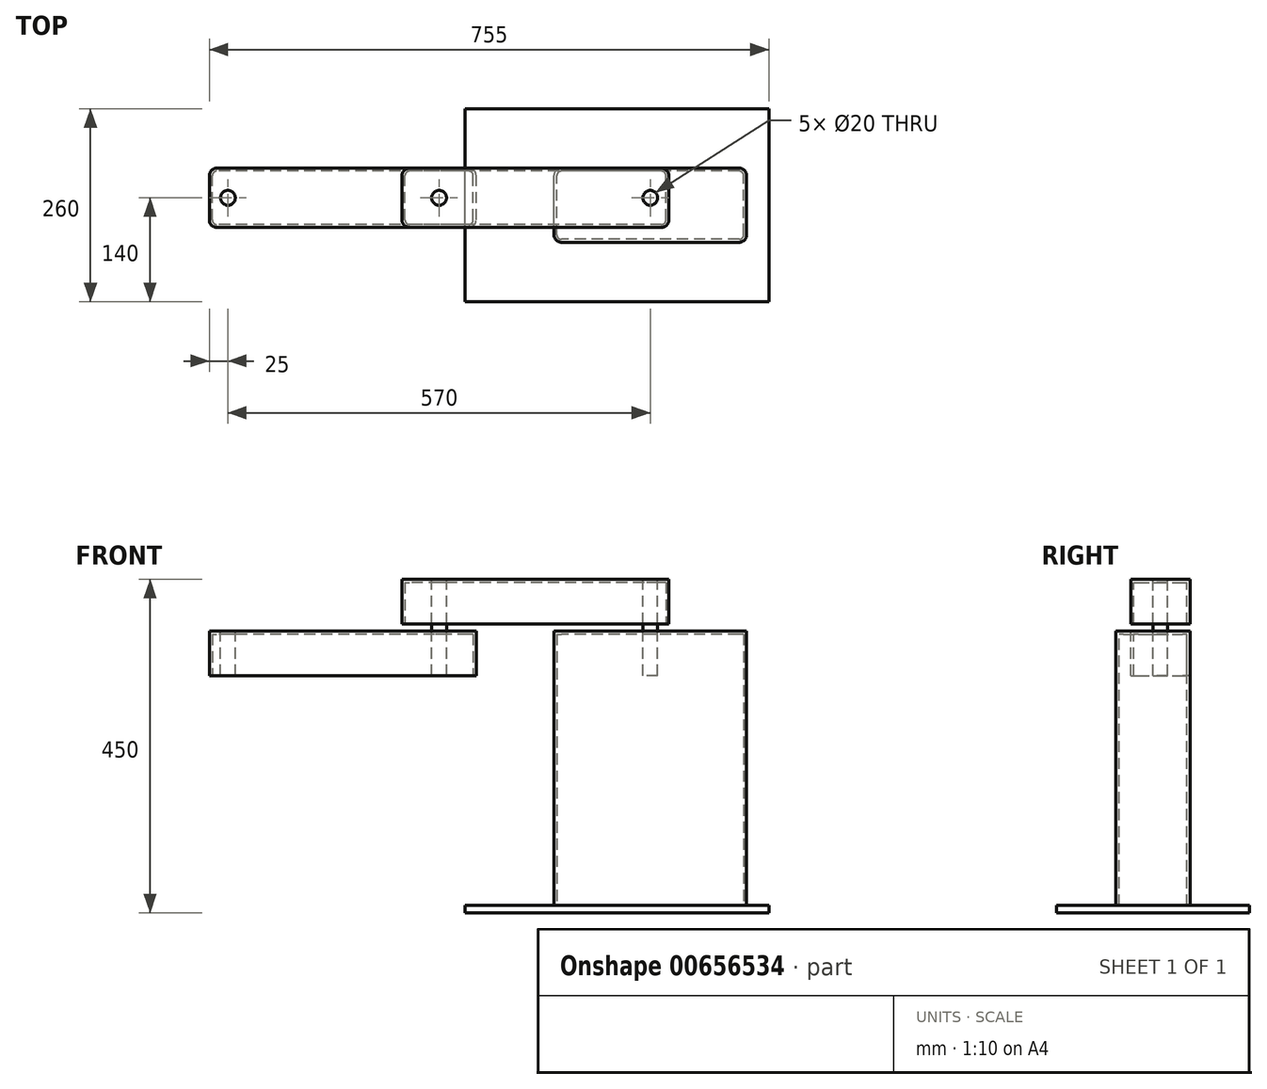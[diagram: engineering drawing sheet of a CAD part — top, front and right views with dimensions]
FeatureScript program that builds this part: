
annotation { "Feature Type Name" : "Feature", "Feature Type Description" : "" }
export const myFeature = defineFeature(function(context is Context, id is Id, definition is map)
    precondition{}
    {
        {
            var Q0;
            Q0=qCreatedBy(makeId("Top.planeOp"),FACE);
            var sketch = newSketch(context, id + "F0", { "sketchPlane" : qUnion([Q0])});
            skLineSegment(sketch, "E0.bottom", {"start": v(180, -40) * mm, "end": v(-180, -40) * mm});
            skLineSegment(sketch, "E0.top", {"start": v(180, 40) * mm, "end": v(-180, 40) * mm});
            skLineSegment(sketch, "E0.left", {"start": v(180, -40) * mm, "end": v(180, 40) * mm});
            skLineSegment(sketch, "E0.right", {"start": v(-180, -40) * mm, "end": v(-180, 40) * mm});
            skPoint(sketch, "E0.middle", {"position": v(0, 0) * mm});
            skPoint(sketch, "E1.center.orphan", {"position": v(-130, 0) * mm});
            skPoint(sketch, "E2.center.orphan", {"position": v(155, 0) * mm});
            skSolve(sketch);
        }
        {
            var Q0;
            Q0=makeQuery(id+"F0.imprint","IMPRINT",FACE,{"disambiguationData":[TD([[makeQuery(id+"F0.imprint","IMPRINT",EDGE,{"derivedFrom":sQuery(id+"F0.wireOp",EDGE,"E0.bottom")}),-1.0]])]});
            extrude(context, id + "F1", {"entities" : qUnion([Q0]), "oppositeDirection" : true, "depth" : 60 * mm, "offsetDistance" : 25 * mm});
        }
        {
            var Q0;
            Q0=makeQuery(id+"F1.opExtrude","CAP_FACE",FACE,{"disambiguationData":[OSD([sQuery(id+"F0.wireOp",EDGE,"E0.bottom"),sQuery(id+"F0.wireOp",EDGE,"E0.top"),sQuery(id+"F0.wireOp",EDGE,"E0.left"),sQuery(id+"F0.wireOp",EDGE,"E0.right"),sQuery(id+"F0.wireOp",EDGE,"E2"),sQuery(id+"F0.wireOp",EDGE,"E1")])],"isStart":true});
            cPlane(context, id + "F2", {"entities" : qUnion([Q0]), "cplaneType" : CPlaneType.OFFSET, "offset" : 70 * mm, "oppositeDirection" : true, "width" : 150 * mm, "height" : 150 * mm});
        }
        {
            var Q0;
            Q0=qCreatedBy(id+"F2.planeOp",FACE);
            var sketch = newSketch(context, id + "F3", { "sketchPlane" : qUnion([Q0])});
            skLineSegment(sketch, "E3.bottom", {"start": v(285, -60) * mm, "end": v(25, -60) * mm});
            skLineSegment(sketch, "E3.top", {"start": v(285, 40) * mm, "end": v(25, 40) * mm});
            skLineSegment(sketch, "E3.left", {"start": v(285, -60) * mm, "end": v(285, 40) * mm});
            skLineSegment(sketch, "E3.right", {"start": v(25, -60) * mm, "end": v(25, 40) * mm});
            skPoint(sketch, "E3.middle", {"position": v(155, -10) * mm});
            skLineSegment(sketch, "E4.0", {"start": v(180, -40) * mm, "end": v(180, 40) * mm, "construction": true});
            skSolve(sketch);
        }
        {
            var Q0;
            Q0=makeQuery(id+"F3.imprint","IMPRINT",FACE,{"disambiguationData":[TD([[makeQuery(id+"F3.imprint","IMPRINT",EDGE,{"derivedFrom":sQuery(id+"F3.wireOp",EDGE,"E3.bottom")}),-1.0]])]});
            extrude(context, id + "F4", {"entities" : qUnion([Q0]), "oppositeDirection" : true, "depth" : 370 * mm, "offsetDistance" : 25 * mm});
        }
        {
            var Q0;
            Q0=makeQuery(id+"F4.opExtrude","CAP_FACE",FACE,{"disambiguationData":[OSD([sQuery(id+"F3.wireOp",EDGE,"E3.bottom"),sQuery(id+"F3.wireOp",EDGE,"E3.top"),sQuery(id+"F3.wireOp",EDGE,"E3.left"),sQuery(id+"F3.wireOp",EDGE,"E3.right")])],"isStart":false});
            var sketch = newSketch(context, id + "F5", { "sketchPlane" : qUnion([Q0])});
            skLineSegment(sketch, "E5.bottom", {"start": v(315, 140) * mm, "end": v(-95, 140) * mm});
            skLineSegment(sketch, "E5.top", {"start": v(315, -120) * mm, "end": v(-95, -120) * mm});
            skLineSegment(sketch, "E5.left", {"start": v(315, 140) * mm, "end": v(315, -120) * mm});
            skLineSegment(sketch, "E5.right", {"start": v(-95, 140) * mm, "end": v(-95, -120) * mm});
            skSolve(sketch);
        }
        {
            var Q0;
            Q0=makeQuery(id+"F5.imprint","IMPRINT",FACE,{"disambiguationData":[TD([[makeQuery(id+"F5.imprint","IMPRINT",EDGE,{"derivedFrom":sQuery(id+"F5.wireOp",EDGE,"E5.bottom")}),1.0]])]});
            var Q1;
            Q1=makeQuery(id+"F5.imprint","IMPRINT",FACE,{"disambiguationData":[TD([[makeQuery(id+"F5.imprint","IMPRINT",EDGE,{"derivedFrom":makeQuery(id+"F4.opExtrude","CAP_EDGE",EDGE,{"disambiguationData":[OSD([sQuery(id+"F3.wireOp",EDGE,"E3.bottom")])],"isStart":false})}),1.0]])]});
            extrude(context, id + "F6", {"entities" : qUnion([Q0, Q1]), "depth" : 10 * mm, "offsetDistance" : 25 * mm});
        }
        {
            var Q0;
            Q0=makeQuery(id+"F4.opExtrude","CAP_FACE",FACE,{"disambiguationData":[OSD([sQuery(id+"F3.wireOp",EDGE,"E3.bottom"),sQuery(id+"F3.wireOp",EDGE,"E3.top"),sQuery(id+"F3.wireOp",EDGE,"E3.left"),sQuery(id+"F3.wireOp",EDGE,"E3.right")])],"isStart":true});
            var sketch = newSketch(context, id + "F7", { "sketchPlane" : qUnion([Q0])});
            skLineSegment(sketch, "E6.bottom", {"start": v(-80, -40) * mm, "end": v(-440, -40) * mm});
            skLineSegment(sketch, "E6.top", {"start": v(-80, 40) * mm, "end": v(-440, 40) * mm});
            skLineSegment(sketch, "E6.left", {"start": v(-80, -40) * mm, "end": v(-80, 40) * mm});
            skLineSegment(sketch, "E6.right", {"start": v(-440, -40) * mm, "end": v(-440, 40) * mm});
            skLineSegment(sketch, "E7.0", {"start": v(-180, -40) * mm, "end": v(-180, 40) * mm, "construction": true});
            skPoint(sketch, "E8.0.center.orphan", {"position": v(-130, 0) * mm});
            skSolve(sketch);
        }
        {
            var Q0;
            Q0=makeQuery(id+"F7.imprint","IMPRINT",FACE,{"disambiguationData":[TD([[makeQuery(id+"F7.imprint","IMPRINT",EDGE,{"derivedFrom":sQuery(id+"F7.wireOp",EDGE,"E6.bottom")}),-1.0]])]});
            extrude(context, id + "F8", {"entities" : qUnion([Q0]), "oppositeDirection" : true, "depth" : 60 * mm, "offsetDistance" : 25 * mm});
        }
        {
            var Q0;
            Q0=makeQuery(id+"F1.opExtrude","CAP_FACE",FACE,{"disambiguationData":[OSD([sQuery(id+"F0.wireOp",EDGE,"E0.bottom"),sQuery(id+"F0.wireOp",EDGE,"E0.top"),sQuery(id+"F0.wireOp",EDGE,"E0.left"),sQuery(id+"F0.wireOp",EDGE,"E0.right")])],"isStart":true});
            var sketch = newSketch(context, id + "F9", { "sketchPlane" : qUnion([Q0])});
            skPoint(sketch, "E9.0", {"position": v(-440, 0) * mm});
            skPoint(sketch, "E10.0", {"position": v(-180, 0) * mm});
            skPoint(sketch, "E11.0", {"position": v(180, 0) * mm});
            skLineSegment(sketch, "E12", {"start": v(-440, 0) * mm, "end": v(180, 0) * mm, "construction": true});
            skCircle(sketch, "E13", {"center": v(-415, 0) * mm, "radius": 10 * mm});
            skCircle(sketch, "E14", {"center": v(-130, 0) * mm, "radius": 10 * mm});
            skCircle(sketch, "E15", {"center": v(155, 0) * mm, "radius": 10 * mm});
            skSolve(sketch);
        }
        {
            var Q0;
            Q0=makeQuery(id+"F8.opExtrude","SWEPT_EDGE",EDGE,{"disambiguationData":[OSD([sQuery(id+"F7.wireOp",EDGE,"E6.bottom"),sQuery(id+"F7.wireOp",EDGE,"E6.right")])]});
            var Q1;
            Q1=makeQuery(id+"F8.opExtrude","SWEPT_EDGE",EDGE,{"disambiguationData":[OSD([sQuery(id+"F7.wireOp",EDGE,"E6.top"),sQuery(id+"F7.wireOp",EDGE,"E6.right")])]});
            var Q2;
            Q2=makeQuery(id+"F8.opExtrude","SWEPT_EDGE",EDGE,{"disambiguationData":[OSD([sQuery(id+"F7.wireOp",EDGE,"E6.top"),sQuery(id+"F7.wireOp",EDGE,"E6.left")])]});
            var Q3;
            Q3=makeQuery(id+"F8.opExtrude","SWEPT_EDGE",EDGE,{"disambiguationData":[OSD([sQuery(id+"F7.wireOp",EDGE,"E6.bottom"),sQuery(id+"F7.wireOp",EDGE,"E6.left")])]});
            var Q4;
            Q4=makeQuery(id+"F1.opExtrude","SWEPT_EDGE",EDGE,{"disambiguationData":[OSD([sQuery(id+"F0.wireOp",EDGE,"E0.bottom"),sQuery(id+"F0.wireOp",EDGE,"E0.right")])]});
            var Q5;
            Q5=makeQuery(id+"F1.opExtrude","SWEPT_EDGE",EDGE,{"disambiguationData":[OSD([sQuery(id+"F0.wireOp",EDGE,"E0.bottom"),sQuery(id+"F0.wireOp",EDGE,"E0.left")])]});
            var Q6;
            Q6=makeQuery(id+"F1.opExtrude","SWEPT_EDGE",EDGE,{"disambiguationData":[OSD([sQuery(id+"F0.wireOp",EDGE,"E0.top"),sQuery(id+"F0.wireOp",EDGE,"E0.left")])]});
            var Q7;
            Q7=makeQuery(id+"F1.opExtrude","SWEPT_EDGE",EDGE,{"disambiguationData":[OSD([sQuery(id+"F0.wireOp",EDGE,"E0.top"),sQuery(id+"F0.wireOp",EDGE,"E0.right")])]});
            var Q8;
            Q8=makeQuery(id+"F4.opExtrude","SWEPT_EDGE",EDGE,{"disambiguationData":[OSD([sQuery(id+"F3.wireOp",EDGE,"E3.top"),sQuery(id+"F3.wireOp",EDGE,"E3.right")])]});
            var Q9;
            Q9=makeQuery(id+"F4.opExtrude","SWEPT_EDGE",EDGE,{"disambiguationData":[OSD([sQuery(id+"F3.wireOp",EDGE,"E3.bottom"),sQuery(id+"F3.wireOp",EDGE,"E3.right")])]});
            var Q10;
            Q10=makeQuery(id+"F4.opExtrude","SWEPT_EDGE",EDGE,{"disambiguationData":[OSD([sQuery(id+"F3.wireOp",EDGE,"E3.top"),sQuery(id+"F3.wireOp",EDGE,"E3.left")])]});
            var Q11;
            Q11=makeQuery(id+"F4.opExtrude","SWEPT_EDGE",EDGE,{"disambiguationData":[OSD([sQuery(id+"F3.wireOp",EDGE,"E3.bottom"),sQuery(id+"F3.wireOp",EDGE,"E3.left")])]});
            fillet(context, id + "F10", {"entities" : qUnion([Q0, Q1, Q2, Q3, Q4, Q5, Q6, Q7, Q8, Q9, Q10, Q11]), "radius" : 10 * mm, "tangentPropagation" : true, "allowEdgeOverflow" : false});
        }
        {
            var Q0;
            Q0=makeQuery(id+"F1.opExtrude","CAP_FACE",FACE,{"disambiguationData":[OSD([sQuery(id+"F0.wireOp",EDGE,"E0.bottom"),sQuery(id+"F0.wireOp",EDGE,"E0.top"),sQuery(id+"F0.wireOp",EDGE,"E0.left"),sQuery(id+"F0.wireOp",EDGE,"E0.right")])],"isStart":false});
            var Q1;
            Q1=makeQuery(id+"F8.opExtrude","CAP_FACE",FACE,{"disambiguationData":[OSD([sQuery(id+"F7.wireOp",EDGE,"E6.bottom"),sQuery(id+"F7.wireOp",EDGE,"E6.top"),sQuery(id+"F7.wireOp",EDGE,"E6.left"),sQuery(id+"F7.wireOp",EDGE,"E6.right")])],"isStart":false});
            var Q2;
            Q2=makeQuery(id+"F4.opExtrude","CAP_FACE",FACE,{"disambiguationData":[OSD([sQuery(id+"F3.wireOp",EDGE,"E3.bottom"),sQuery(id+"F3.wireOp",EDGE,"E3.top"),sQuery(id+"F3.wireOp",EDGE,"E3.left"),sQuery(id+"F3.wireOp",EDGE,"E3.right")])],"isStart":false});
            var Q3;
            Q3=makeQuery(id+"F8.opExtrude","SWEPT_BODY",BODY,{"disambiguationData":[OSD([sQuery(id+"F7.wireOp",EDGE,"E6.bottom"),sQuery(id+"F7.wireOp",EDGE,"E6.top"),sQuery(id+"F7.wireOp",EDGE,"E6.left"),sQuery(id+"F7.wireOp",EDGE,"E6.right")])]});
            var Q4;
            Q4=makeQuery(id+"F1.opExtrude","SWEPT_BODY",BODY,{"disambiguationData":[OSD([sQuery(id+"F0.wireOp",EDGE,"E0.bottom"),sQuery(id+"F0.wireOp",EDGE,"E0.top"),sQuery(id+"F0.wireOp",EDGE,"E0.left"),sQuery(id+"F0.wireOp",EDGE,"E0.right")])]});
            var Q5;
            Q5=makeQuery(id+"F4.opExtrude","SWEPT_BODY",BODY,{"disambiguationData":[OSD([sQuery(id+"F3.wireOp",EDGE,"E3.bottom"),sQuery(id+"F3.wireOp",EDGE,"E3.top"),sQuery(id+"F3.wireOp",EDGE,"E3.left"),sQuery(id+"F3.wireOp",EDGE,"E3.right")])]});
            shell(context, id + "F11", {"entities" : qUnion([Q0, Q1, Q2]), "parts" : qUnion([Q3, Q4, Q5]), "thickness" : 4 * mm});
        }
        {
            var Q0;
            Q0=makeQuery(id+"F9.imprint","IMPRINT",FACE,{"disambiguationData":[TD([[makeQuery(id+"F9.imprint","IMPRINT",EDGE,{"derivedFrom":sQuery(id+"F9.wireOp",EDGE,"E13")}),1.0]])]});
            var Q1;
            Q1=makeQuery(id+"F9.imprint","IMPRINT",FACE,{"disambiguationData":[TD([[makeQuery(id+"F9.imprint","IMPRINT",EDGE,{"derivedFrom":sQuery(id+"F9.wireOp",EDGE,"E14")}),1.0]])]});
            var Q2;
            Q2=makeQuery(id+"F9.imprint","IMPRINT",FACE,{"disambiguationData":[TD([[makeQuery(id+"F9.imprint","IMPRINT",EDGE,{"derivedFrom":sQuery(id+"F9.wireOp",EDGE,"E15")}),1.0]])]});
            extrude(context, id + "F12", {"entities" : qUnion([Q0, Q1, Q2]), "operationType" : NewBodyOperationType.REMOVE, "oppositeDirection" : true, "depth" : 130 * mm, "offsetDistance" : 25 * mm});
        }
        {
            var Q0;
            Q0=makeQuery(id+"F9.imprint","IMPRINT",FACE,{"disambiguationData":[TD([[makeQuery(id+"F9.imprint","IMPRINT",EDGE,{"derivedFrom":sQuery(id+"F9.wireOp",EDGE,"E14")}),1.0]])]});
            var Q1;
            Q1=makeQuery(id+"F9.imprint","IMPRINT",FACE,{"disambiguationData":[TD([[makeQuery(id+"F9.imprint","IMPRINT",EDGE,{"derivedFrom":sQuery(id+"F9.wireOp",EDGE,"E15")}),1.0]])]});
            extrude(context, id + "F13", {"entities" : qUnion([Q0, Q1]), "oppositeDirection" : true, "depth" : 130 * mm, "offsetDistance" : 25 * mm});
        }
        {
            var Q0;
            Q0=makeQuery(id+"F8.opExtrude","CAP_FACE",FACE,{"disambiguationData":[OSD([sQuery(id+"F7.wireOp",EDGE,"E6.bottom"),sQuery(id+"F7.wireOp",EDGE,"E6.top"),sQuery(id+"F7.wireOp",EDGE,"E6.left"),sQuery(id+"F7.wireOp",EDGE,"E6.right")])],"isStart":true});
            var sketch = newSketch(context, id + "F14", { "sketchPlane" : qUnion([Q0])});
            skCircle(sketch, "E16.0", {"center": v(-415, 0) * mm, "radius": 10 * mm});
            skSolve(sketch);
        }
        {
            var Q0;
            Q0=makeQuery(id+"F14.imprint","IMPRINT",FACE,{"disambiguationData":[TD([[makeQuery(id+"F14.imprint","IMPRINT",EDGE,{"derivedFrom":sQuery(id+"F14.wireOp",EDGE,"E16.0")}),1.0]])]});
            extrude(context, id + "F15", {"entities" : qUnion([Q0]), "oppositeDirection" : true, "depth" : 60 * mm, "offsetDistance" : 25 * mm});
        }
        {
            var Q0;
            Q0=makeQuery(id+"F1.opExtrude","CAP_FACE",FACE,{"disambiguationData":[OSD([sQuery(id+"F0.wireOp",EDGE,"E0.bottom"),sQuery(id+"F0.wireOp",EDGE,"E0.top"),sQuery(id+"F0.wireOp",EDGE,"E0.left"),sQuery(id+"F0.wireOp",EDGE,"E0.right")])],"isStart":true});
            var sketch = newSketch(context, id + "F16", { "sketchPlane" : qUnion([Q0])});
            skPoint(sketch, "E17.0", {"position": v(-180, 0) * mm});
            skPoint(sketch, "E18.0", {"position": v(180, 0) * mm});
            skPoint(sketch, "E19.0", {"position": v(-440, 0) * mm});
            skCircle(sketch, "E20", {"center": v(-130, 0) * mm, "radius": 15 * mm});
            skCircle(sketch, "E21", {"center": v(-130, 0) * mm, "radius": 10 * mm});
            skLineSegment(sketch, "E22", {"start": v(-272.5, 21.3) * mm, "end": v(-272.5, -21.88) * mm, "construction": true});
            skLineSegment(sketch, "E23", {"start": v(12.5, 23.23) * mm, "end": v(12.5, -20.6) * mm, "construction": true});
            skCircle(sketch, "E24.0", {"center": v(-415, 0) * mm, "radius": 10 * mm, "construction": true});
            skCircle(sketch, "E25.0", {"center": v(155, 0) * mm, "radius": 10 * mm, "construction": true});
            skCircle(sketch, "E26.MirrorC", {"center": v(155, 0) * mm, "radius": 10 * mm});
            skCircle(sketch, "E27.MirrorC", {"center": v(155, 0) * mm, "radius": 15 * mm});
            skCircle(sketch, "E28.MirrorC", {"center": v(-415, 0) * mm, "radius": 15 * mm});
            skCircle(sketch, "E29.MirrorC", {"center": v(-415, 0) * mm, "radius": 10 * mm});
            skSolve(sketch);
        }
        {
            var Q0;
            Q0=makeQuery(id+"F1.opExtrude","CAP_FACE",FACE,{"disambiguationData":[OSD([sQuery(id+"F0.wireOp",EDGE,"E0.bottom"),sQuery(id+"F0.wireOp",EDGE,"E0.top"),sQuery(id+"F0.wireOp",EDGE,"E0.left"),sQuery(id+"F0.wireOp",EDGE,"E0.right")])],"isStart":true});
            var sketch = newSketch(context, id + "F17", { "sketchPlane" : qUnion([Q0])});
            skCircle(sketch, "E30.0", {"center": v(-130, 0) * mm, "radius": 10 * mm});
            skCircle(sketch, "E31.0", {"center": v(-130, 0) * mm, "radius": 15 * mm});
            skCircle(sketch, "E32.0", {"center": v(155, 0) * mm, "radius": 10 * mm});
            skCircle(sketch, "E33.0", {"center": v(155, 0) * mm, "radius": 15 * mm});
            skSolve(sketch);
        }
        {
            var Q0;
            Q0=makeQuery(id+"F8.opExtrude","CAP_FACE",FACE,{"disambiguationData":[OSD([sQuery(id+"F7.wireOp",EDGE,"E6.bottom"),sQuery(id+"F7.wireOp",EDGE,"E6.top"),sQuery(id+"F7.wireOp",EDGE,"E6.left"),sQuery(id+"F7.wireOp",EDGE,"E6.right")])],"isStart":true});
            var sketch = newSketch(context, id + "F18", { "sketchPlane" : qUnion([Q0])});
            skCircle(sketch, "E34.0", {"center": v(-415, 0) * mm, "radius": 15 * mm});
            skCircle(sketch, "E35.0", {"center": v(-415, 0) * mm, "radius": 10 * mm});
            skCircle(sketch, "E36.0", {"center": v(-130, 0) * mm, "radius": 15 * mm});
            skCircle(sketch, "E37.0", {"center": v(-130, 0) * mm, "radius": 10 * mm});
            skSolve(sketch);
        }
        {
            var Q0;
            Q0=makeQuery(id+"F8.opExtrude","CAP_FACE",FACE,{"disambiguationData":[OSD([sQuery(id+"F7.wireOp",EDGE,"E6.bottom"),sQuery(id+"F7.wireOp",EDGE,"E6.top"),sQuery(id+"F7.wireOp",EDGE,"E6.left"),sQuery(id+"F7.wireOp",EDGE,"E6.right")])],"isStart":false});
            cPlane(context, id + "F19", {"entities" : qUnion([Q0]), "cplaneType" : CPlaneType.OFFSET, "offset" : 23 * mm, "oppositeDirection" : true, "width" : 150 * mm, "height" : 150 * mm});
        }
        {
            var Q0;
            Q0=qCreatedBy(id+"F19.planeOp",FACE);
            var sketch = newSketch(context, id + "F20", { "sketchPlane" : qUnion([Q0])});
            skCircle(sketch, "E38.0", {"center": v(-130, 0) * mm, "radius": 10 * mm});
            skCircle(sketch, "E39", {"center": v(-130, 0) * mm, "radius": 17.5 * mm});
            skSolve(sketch);
        }
        {
            var Q0;
            Q0=makeQuery(id+"F20.imprint","IMPRINT",FACE,{"disambiguationData":[TD([[makeQuery(id+"F20.imprint","IMPRINT",EDGE,{"derivedFrom":sQuery(id+"F20.wireOp",EDGE,"E38.0")}),-1.0]])]});
            extrude(context, id + "F21", {"entities" : qUnion([Q0]), "oppositeDirection" : true, "depth" : 10 * mm, "offsetDistance" : 25 * mm});
        }
        {
            var Q0;
            Q0=makeQuery(id+"F21.opExtrude","SWEPT_BODY",BODY,{"disambiguationData":[OSD([sQuery(id+"F20.wireOp",EDGE,"E38.0"),sQuery(id+"F20.wireOp",EDGE,"E39")])]});
            var Q1;
            Q1=makeQuery(id+"FecXoAADy8eqeZi_10.opExtrude","SWEPT_BODY",BODY,{"disambiguationData":[OSD([sQuery(id+"F18.wireOp",EDGE,"E36.0"),sQuery(id+"F18.wireOp",EDGE,"E37.0")])]});
            deleteBodies(context, id + "F22", {"entities" : qUnion([Q0, Q1])});
        }
    });
